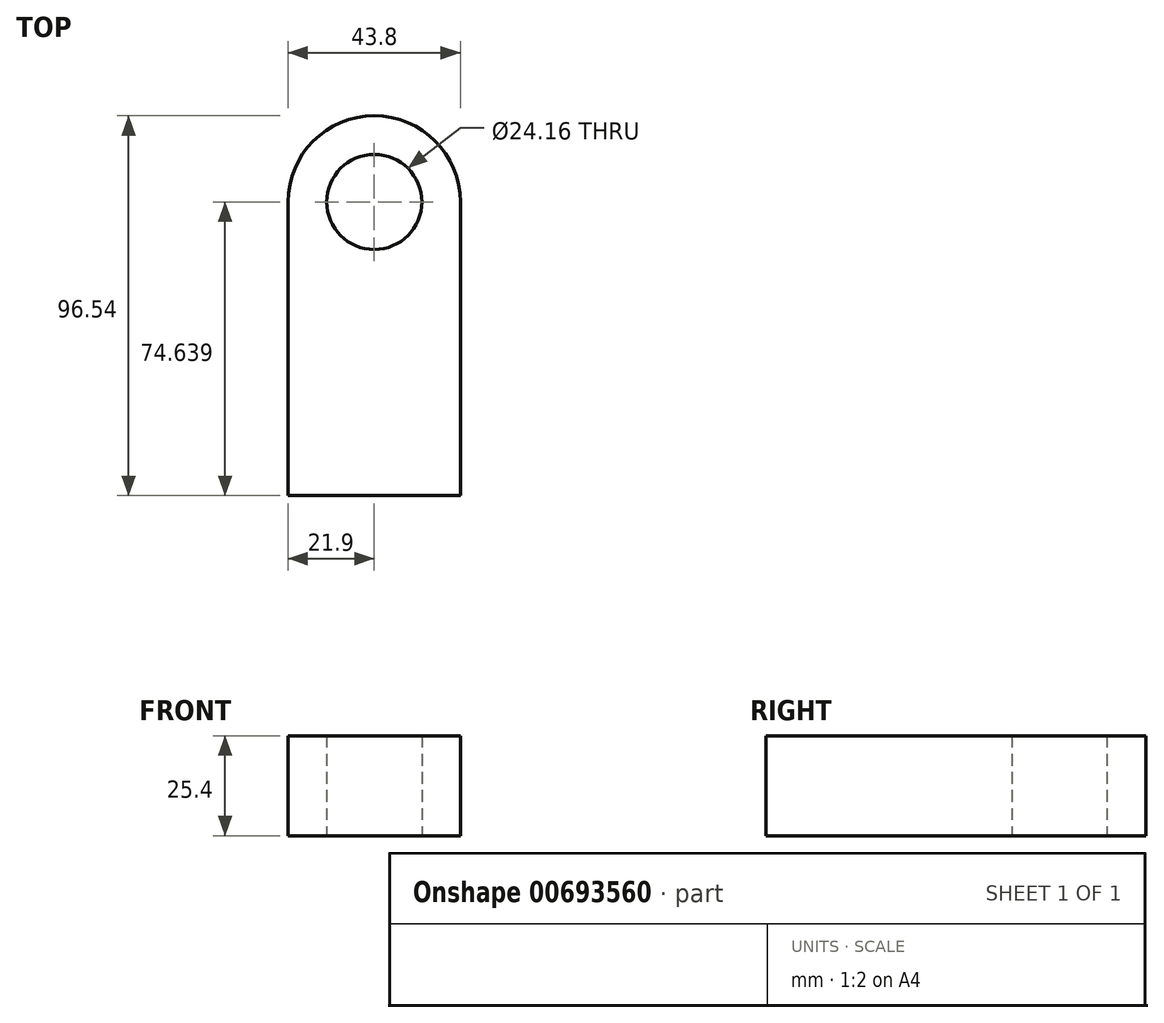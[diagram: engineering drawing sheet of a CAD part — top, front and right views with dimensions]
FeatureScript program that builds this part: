
annotation { "Feature Type Name" : "Feature", "Feature Type Description" : "" }
export const myFeature = defineFeature(function(context is Context, id is Id, definition is map)
    precondition{}
    {
        {
            var Q0;
            Q0=qCreatedBy(makeId("Top.planeOp"),FACE);
            var sketch = newSketch(context, id + "F0", { "sketchPlane" : qUnion([Q0])});
            skLineSegment(sketch, "E0.top", {"start": v(21.9, -37.32) * mm, "end": v(-21.9, -37.32) * mm});
            skLineSegment(sketch, "E0.left", {"start": v(21.9, 37.32) * mm, "end": v(21.9, -37.32) * mm});
            skLineSegment(sketch, "E0.right", {"start": v(-21.9, 37.32) * mm, "end": v(-21.9, -37.32) * mm});
            skPoint(sketch, "E0.middle", {"position": v(0, 0) * mm});
            skArc(sketch, "E1", {"start": v(21.9, 37.32) * mm, "mid": v(0, 59.22) * mm, "end": v(-21.9, 37.32) * mm});
            skCircle(sketch, "E2", {"center": v(0, 37.32) * mm, "radius": 12.08 * mm});
            skSolve(sketch);
        }
        {
            var Q0;
            Q0=makeQuery(id+"F0.imprint","IMPRINT",FACE,{"disambiguationData":[TD([[makeQuery(id+"F0.imprint","IMPRINT",EDGE,{"derivedFrom":sQuery(id+"F0.wireOp",EDGE,"E0.top")}),-1.0]])]});
            extrude(context, id + "F1", {"entities" : qUnion([Q0]), "depth" : 25.4 * mm, "offsetDistance" : 25.4 * mm});
        }
    });
